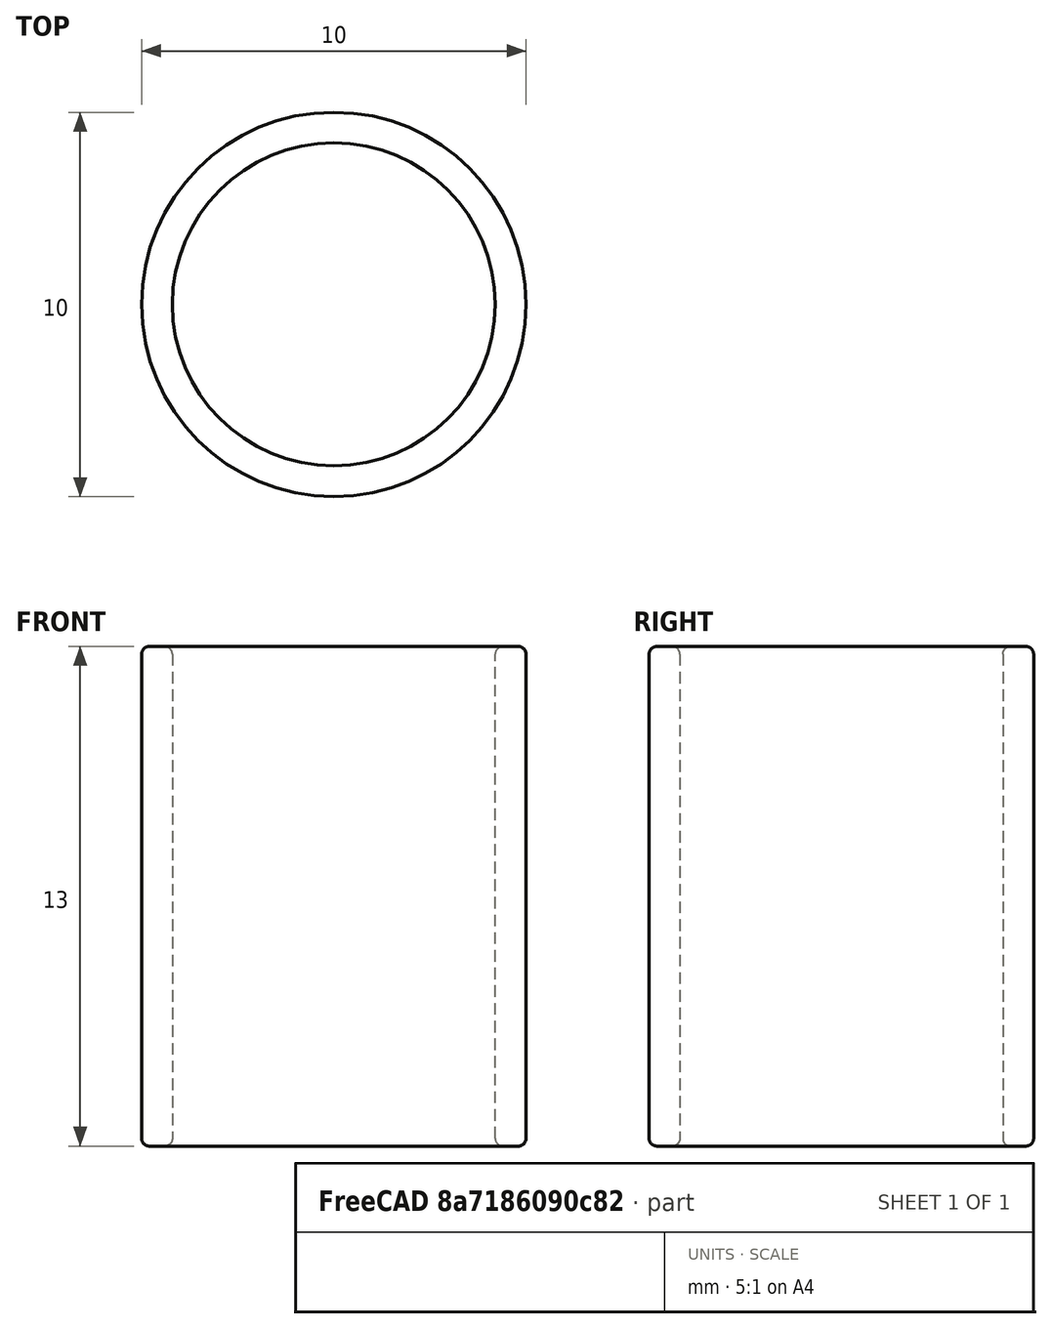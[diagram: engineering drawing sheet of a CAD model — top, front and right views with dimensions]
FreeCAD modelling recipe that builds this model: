
FCSTD DOCUMENT  (FreeCAD 0.21R33694 (Git))
Label: Tube V 8.3 int led tete ronde
License: All rights reserved
LicenseURL: http://en.wikipedia.org/wiki/All_rights_reserved
objects: PartDesign::Fillet×2, Sketcher::SketchObject×1, PartDesign::Pad×1, PartDesign::Body×1
note: 8 computed .brp shape members not serialized (recipe doc carries the construction recipe); baked Part::Feature solids carry a one-line shape summary decoded from their .brp

FEATURE [Sketcher::SketchObject] Sketch
  FullyConstrained = false
  MapMode = 5
  Support = -> [XY_Plane]
  sketch-geometry (2):
    g0: Circle CenterX=0 CenterY=0 CenterZ=0 NormalX=0 NormalY=0 NormalZ=1 AngleXU=0 Radius=4.2
    g1: Circle CenterX=0 CenterY=0 CenterZ=0 NormalX=0 NormalY=0 NormalZ=1 AngleXU=0 Radius=5
  constraints (2):
    c: Diameter(g0) = 8.4
    c: Diameter(g1) = 10
FEATURE [PartDesign::Pad] Pad
  AllowMultiFace = false
  Direction = (0,0,1)
  Length = 13
  Length2 = 100
  Profile = -> Sketch
  ReferenceAxis = -> Sketch [N_Axis]
  Type = 0
FEATURE [PartDesign::Fillet] Fillet
  Base = -> Pad [Face3]
  BaseFeature = -> Pad
  Radius = 0.2
  Refine = true
  SupportTransform = false
  UseAllEdges = false
FEATURE [PartDesign::Fillet] Fillet001
  Base = -> Fillet [Face3]
  BaseFeature = -> Fillet
  Radius = 0.2
  Refine = true
  SupportTransform = false
  UseAllEdges = false
FEATURE [PartDesign::Body] Body
  Group = -> [Sketch,Pad,Fillet,Fillet001]
  Origin = -> Origin
  Tip = -> Fillet001
